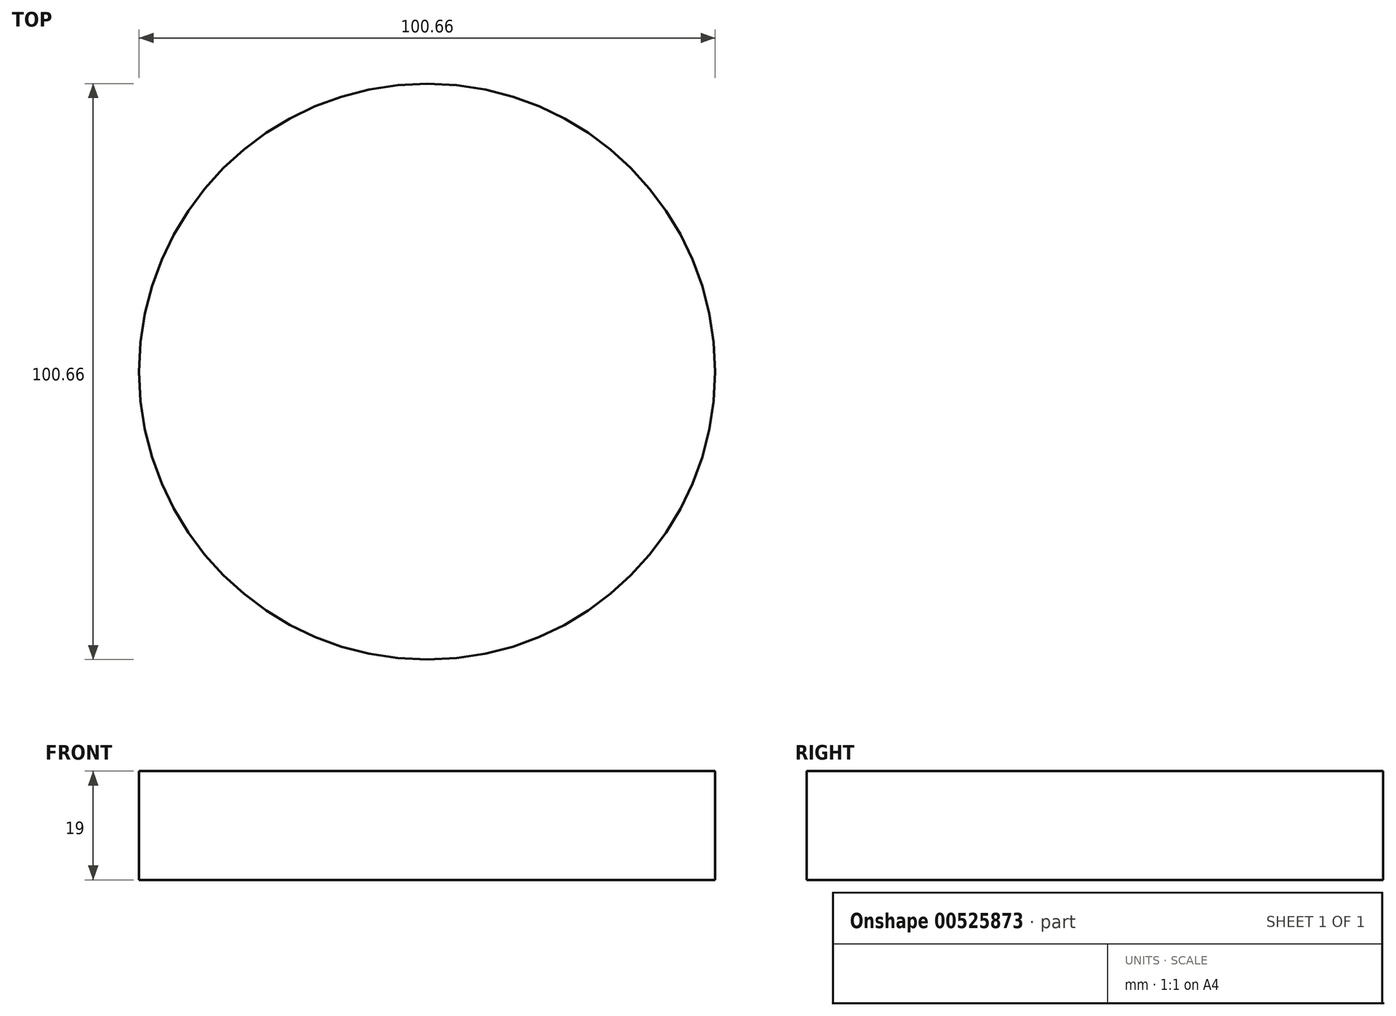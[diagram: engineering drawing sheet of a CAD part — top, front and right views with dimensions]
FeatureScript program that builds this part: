
annotation { "Feature Type Name" : "Feature", "Feature Type Description" : "" }
export const myFeature = defineFeature(function(context is Context, id is Id, definition is map)
    precondition{}
    {
        {
            var Q0;
            Q0=qCreatedBy(makeId("Top.planeOp"),FACE);
            var sketch = newSketch(context, id + "F0", { "sketchPlane" : qUnion([Q0])});
            skCircle(sketch, "E0", {"center": v(0, 0) * mm, "radius": 50.33 * mm});
            skSolve(sketch);
        }
        {
            var Q0;
            Q0 = qSketchRegion(id + "F0", true);
            extrude(context, id + "F1", {"entities" : qUnion([Q0]), "depth" : 19 * mm, "offsetDistance" : 25 * mm});
        }
    });
